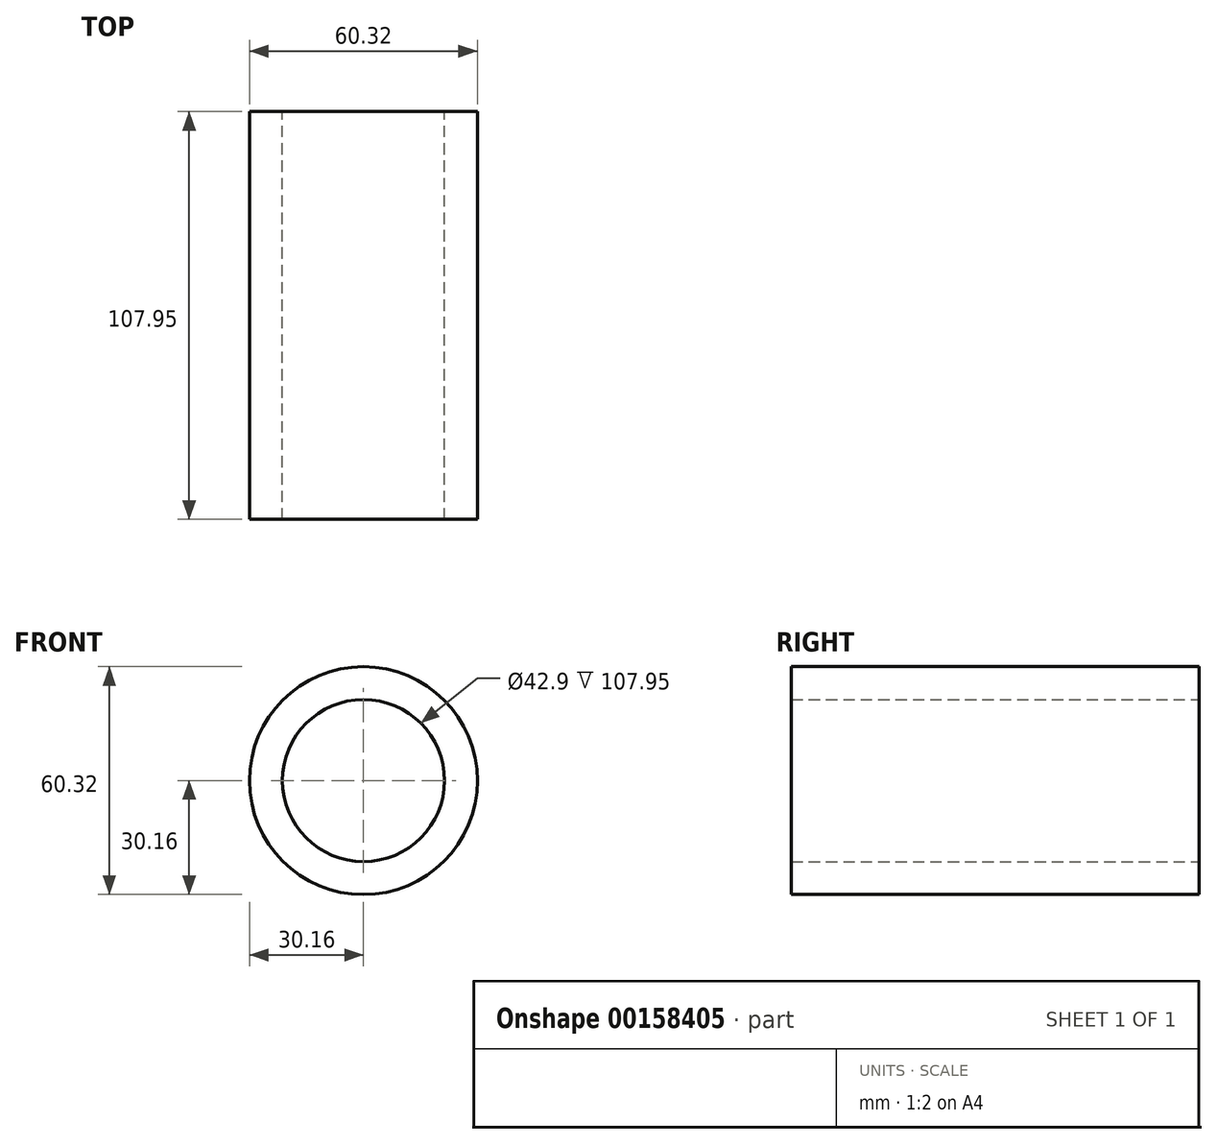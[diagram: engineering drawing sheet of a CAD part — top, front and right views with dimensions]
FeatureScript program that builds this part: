
annotation { "Feature Type Name" : "Feature", "Feature Type Description" : "" }
export const myFeature = defineFeature(function(context is Context, id is Id, definition is map)
    precondition{}
    {
        {
            var Q0;
            Q0=qCreatedBy(makeId("Front.planeOp"),FACE);
            var sketch = newSketch(context, id + "F0", { "sketchPlane" : qUnion([Q0])});
            skCircle(sketch, "E0", {"center": v(0, 0) * mm, "radius": 30.16 * mm});
            skCircle(sketch, "E1.0", {"center": v(0, 0) * mm, "radius": 21.45 * mm});
            skSolve(sketch);
        }
        {
            var Q0;
            Q0=makeQuery(id+"F0.imprint","IMPRINT",FACE,{"disambiguationData":[TD([[makeQuery(id+"F0.imprint","IMPRINT",EDGE,{"derivedFrom":sQuery(id+"F0.wireOp",EDGE,"E0")}),1.0]])]});
            extrude(context, id + "F1", {"entities" : qUnion([Q0]), "depth" : 107.95 * mm});
        }
    });
